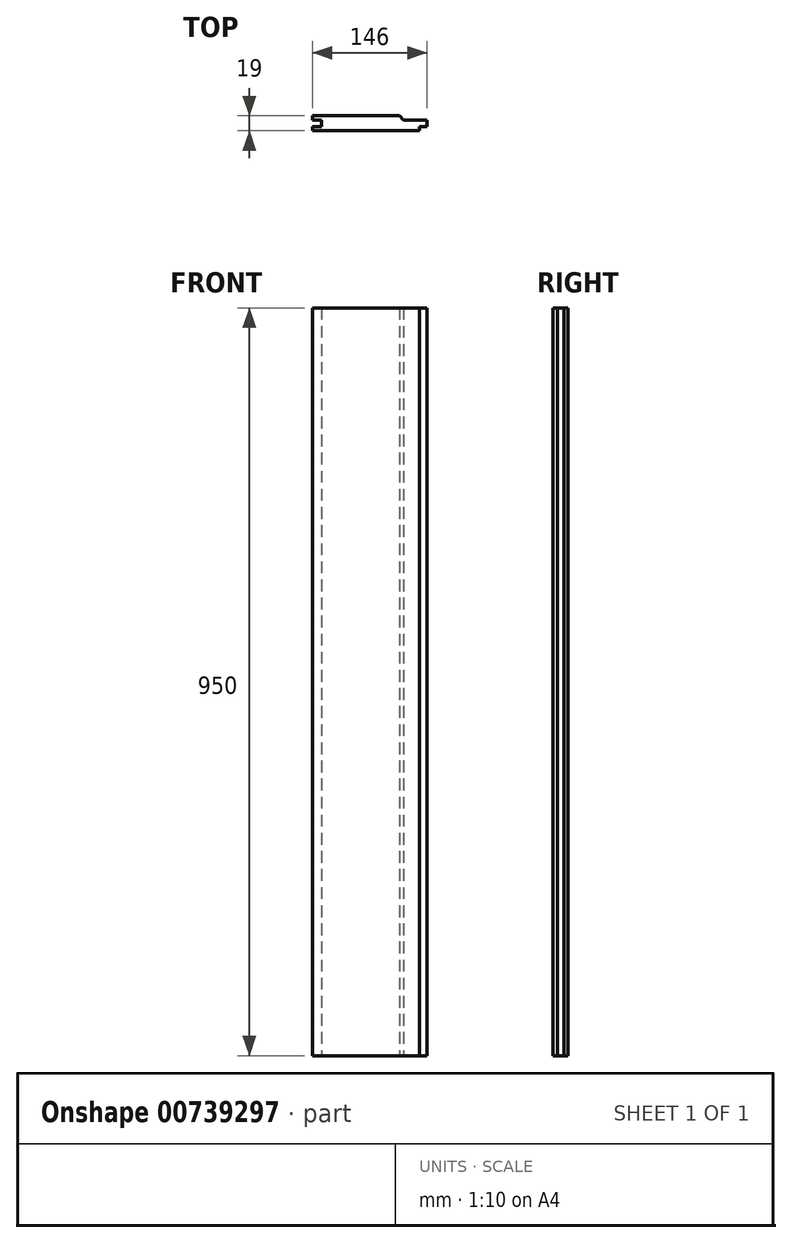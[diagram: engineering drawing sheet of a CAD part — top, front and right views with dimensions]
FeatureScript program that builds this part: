
annotation { "Feature Type Name" : "Feature", "Feature Type Description" : "" }
export const myFeature = defineFeature(function(context is Context, id is Id, definition is map)
    precondition{}
    {
        {
            var Q0;
            Q0=qCreatedBy(makeId("Top.planeOp"),FACE);
            var sketch = newSketch(context, id + "F0", { "sketchPlane" : qUnion([Q0])});
            skLineSegment(sketch, "E0.bottom", {"start": v(0, -9.5) * mm, "end": v(136, -9.5) * mm});
            skLineSegment(sketch, "E0.top", {"start": v(0, 9.5) * mm, "end": v(110.5, 9.5) * mm});
            skLineSegment(sketch, "E0.left", {"start": v(0, -9.5) * mm, "end": v(0, -4) * mm});
            skLineSegment(sketch, "E0.right", {"start": v(136, -9.5) * mm, "end": v(136, -4) * mm});
            skLineSegment(sketch, "E1", {"start": v(0, -4) * mm, "end": v(12, -4) * mm});
            skLineSegment(sketch, "E2", {"start": v(12, -4) * mm, "end": v(12, 4) * mm});
            skLineSegment(sketch, "E3", {"start": v(12, 4) * mm, "end": v(0, 4) * mm});
            skLineSegment(sketch, "E4.trimOffspring", {"start": v(0, 4) * mm, "end": v(0, 9.5) * mm});
            skLineSegment(sketch, "E5", {"start": v(136, -4) * mm, "end": v(146, -4) * mm});
            skLineSegment(sketch, "E6", {"start": v(146, -4) * mm, "end": v(146, 4) * mm});
            skLineSegment(sketch, "E7", {"start": v(146, 4) * mm, "end": v(116, 4) * mm});
            skLineSegment(sketch, "E8.trimOffspring", {"start": v(116, 4) * mm, "end": v(110.5, 9.5) * mm});
            skSolve(sketch);
        }
        {
            var Q0;
            Q0=makeQuery(id+"F0.imprint","IMPRINT",FACE,{"disambiguationData":[TD([[makeQuery(id+"F0.imprint","IMPRINT",EDGE,{"derivedFrom":sQuery(id+"F0.wireOp",EDGE,"E0.bottom")}),1.0]])]});
            extrude(context, id + "F1", {"entities" : qUnion([Q0]), "depth" : 950 * mm, "offsetDistance" : 25 * mm});
        }
    });
